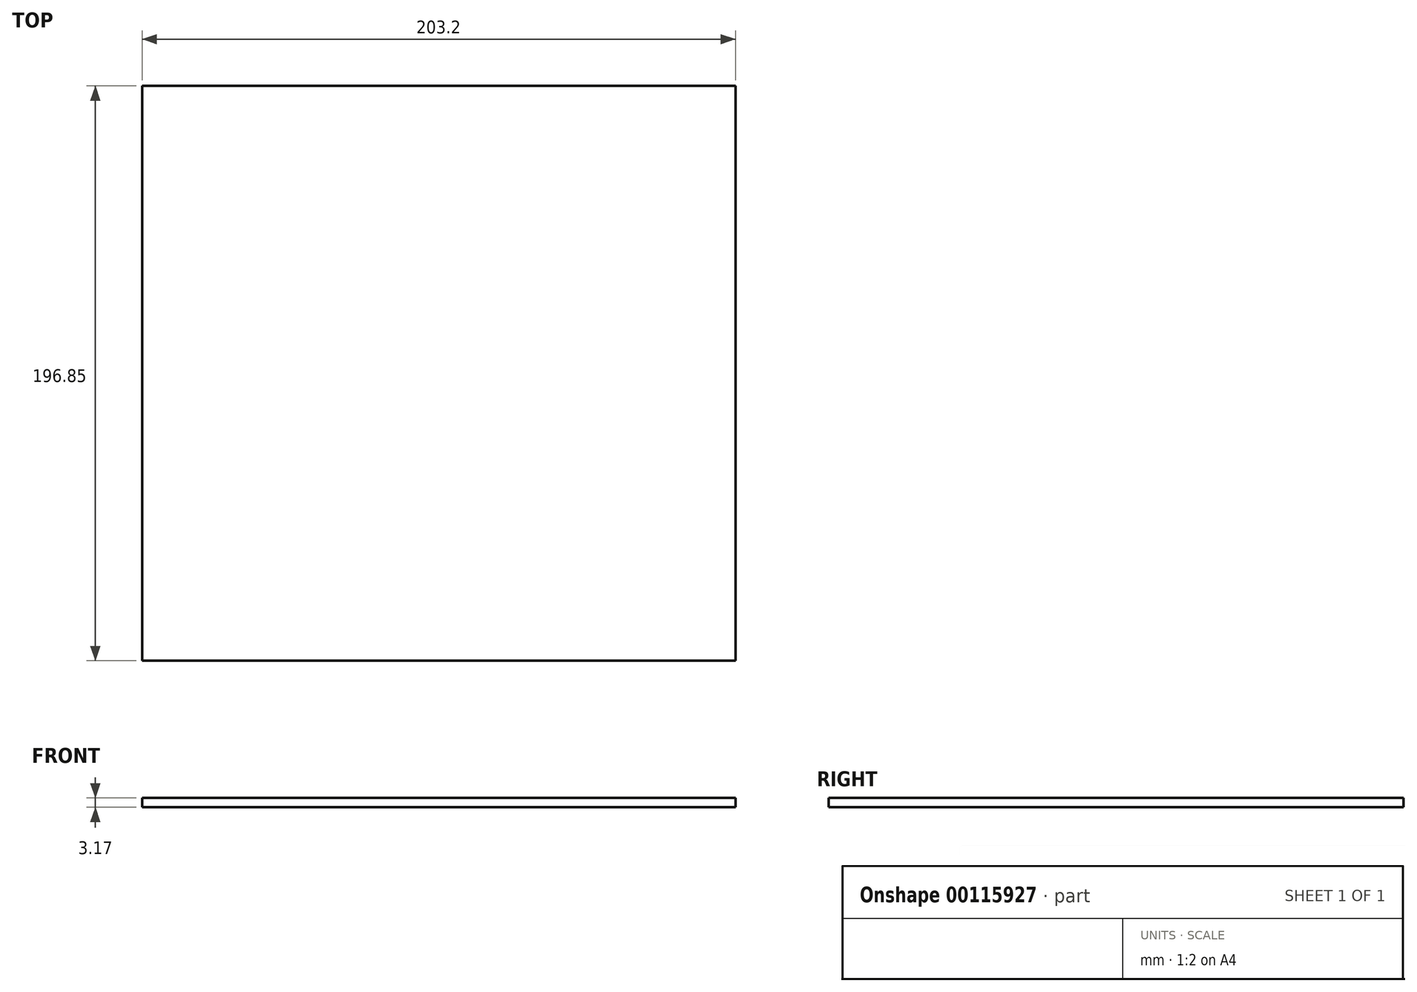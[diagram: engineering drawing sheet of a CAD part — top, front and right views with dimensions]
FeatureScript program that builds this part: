
annotation { "Feature Type Name" : "Feature", "Feature Type Description" : "" }
export const myFeature = defineFeature(function(context is Context, id is Id, definition is map)
    precondition{}
    {
        {
            var Q0;
            Q0=qCreatedBy(makeId("Top.planeOp"),FACE);
            var sketch = newSketch(context, id + "F0", { "sketchPlane" : qUnion([Q0])});
            skLineSegment(sketch, "E0.bottom", {"start": v(-111.63, 128.48) * mm, "end": v(91.57, 128.48) * mm});
            skLineSegment(sketch, "E0.top", {"start": v(-111.63, -68.37) * mm, "end": v(91.57, -68.37) * mm});
            skLineSegment(sketch, "E0.left", {"start": v(-111.63, 128.48) * mm, "end": v(-111.63, -68.37) * mm});
            skLineSegment(sketch, "E0.right", {"start": v(91.57, 128.48) * mm, "end": v(91.57, -68.37) * mm});
            skSolve(sketch);
        }
        {
            var Q0;
            Q0=makeQuery(id+"F0.imprint","IMPRINT",FACE,{"disambiguationData":[TD([[makeQuery(id+"F0.imprint","IMPRINT",EDGE,{"derivedFrom":sQuery(id+"F0.wireOp",EDGE,"E0.bottom")}),-1.0]])]});
            extrude(context, id + "F1", {"entities" : qUnion([Q0]), "depth" : 3.17 * mm});
        }
    });
